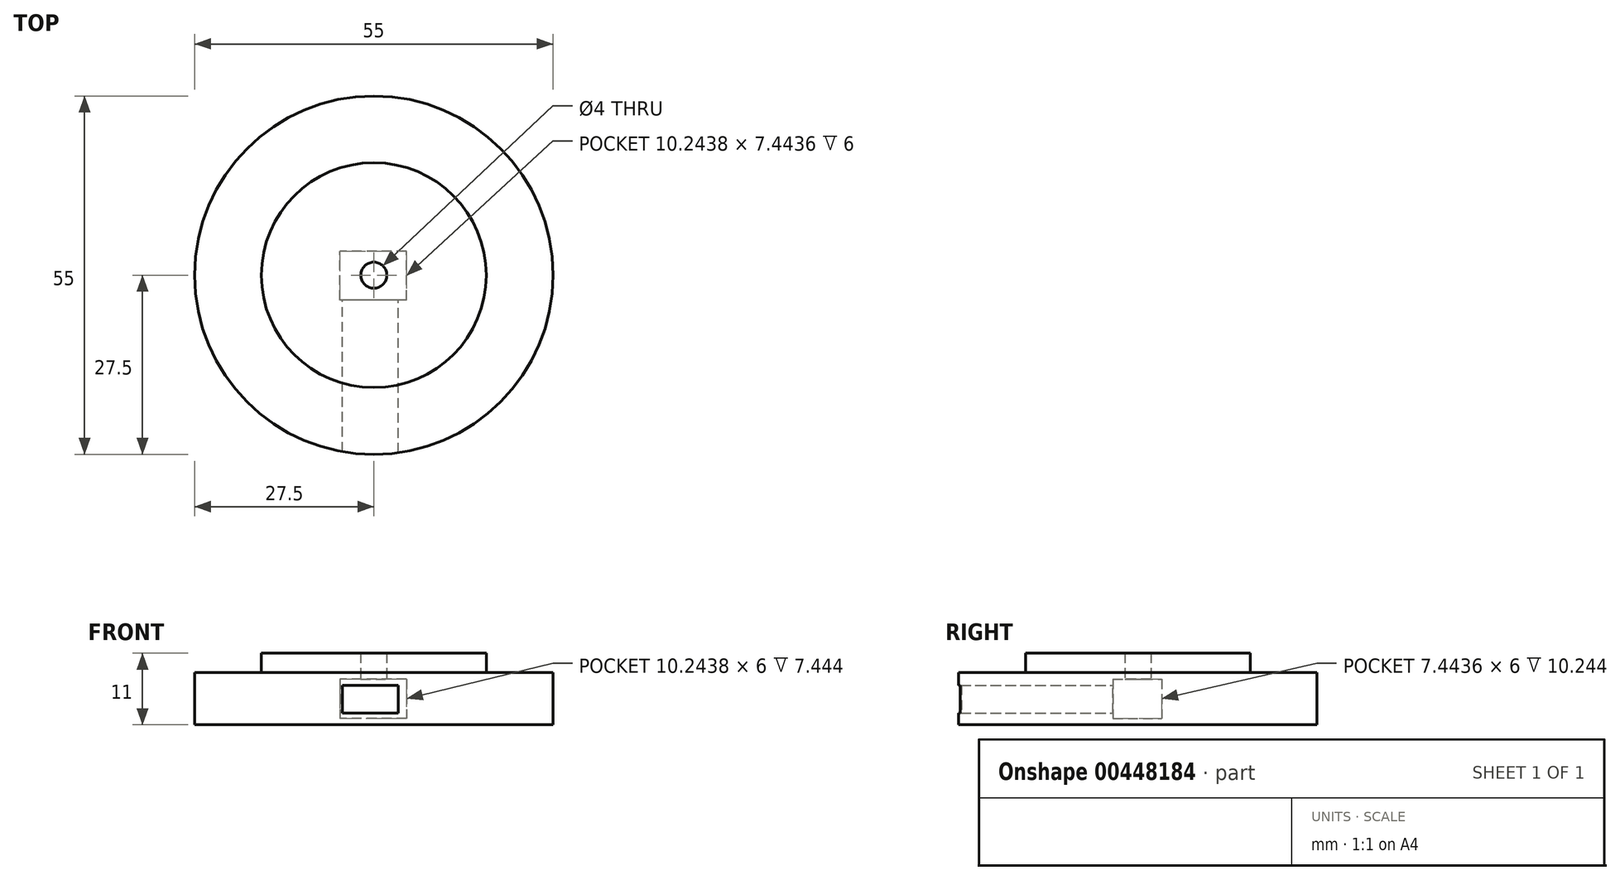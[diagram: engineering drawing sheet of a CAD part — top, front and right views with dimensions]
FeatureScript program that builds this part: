
annotation { "Feature Type Name" : "Feature", "Feature Type Description" : "" }
export const myFeature = defineFeature(function(context is Context, id is Id, definition is map)
    precondition{}
    {
        {
            var Q0;
            Q0=qCreatedBy(makeId("Top.planeOp"),FACE);
            var sketch = newSketch(context, id + "F0", { "sketchPlane" : qUnion([Q0])});
            skCircle(sketch, "E0", {"center": v(0, 0) * mm, "radius": 27.5 * mm});
            skSolve(sketch);
        }
        {
            var Q0;
            Q0=makeQuery(id+"F0.imprint","IMPRINT",FACE,{"disambiguationData":[TD([[makeQuery(id+"F0.imprint","IMPRINT",EDGE,{"derivedFrom":sQuery(id+"F0.wireOp",EDGE,"E0")}),1.0]])]});
            extrude(context, id + "F1", {"entities" : qUnion([Q0]), "depth" : 8 * mm});
        }
        {
            var Q0;
            Q0=makeQuery(id+"F1.opExtrude","CAP_FACE",FACE,{"disambiguationData":[OSD([sQuery(id+"F0.wireOp",EDGE,"E0")])],"isStart":false});
            var sketch = newSketch(context, id + "F2", { "sketchPlane" : qUnion([Q0])});
            skCircle(sketch, "E1", {"center": v(0, 0) * mm, "radius": 17.25 * mm});
            skSolve(sketch);
        }
        {
            var Q0;
            Q0=makeQuery(id+"F2.imprint","IMPRINT",FACE,{"disambiguationData":[TD([[makeQuery(id+"F2.imprint","IMPRINT",EDGE,{"derivedFrom":sQuery(id+"F2.wireOp",EDGE,"E1")}),1.0]])]});
            extrude(context, id + "F3", {"entities" : qUnion([Q0]), "operationType" : NewBodyOperationType.ADD, "depth" : 3 * mm});
        }
        {
            var Q0;
            Q0=makeQuery(id+"F1.opExtrude","CAP_FACE",FACE,{"disambiguationData":[OSD([sQuery(id+"F0.wireOp",EDGE,"E0")])],"isStart":true});
            var sketch = newSketch(context, id + "F4", { "sketchPlane" : qUnion([Q0])});
            skLineSegment(sketch, "E2.bottom", {"start": v(5.02, 3.8) * mm, "end": v(-5.22, 3.8) * mm});
            skLineSegment(sketch, "E2.top", {"start": v(5.02, -3.64) * mm, "end": v(-5.22, -3.64) * mm});
            skLineSegment(sketch, "E2.left", {"start": v(5.02, 3.8) * mm, "end": v(5.02, -3.64) * mm});
            skLineSegment(sketch, "E2.right", {"start": v(-5.22, 3.8) * mm, "end": v(-5.22, -3.64) * mm});
            skSolve(sketch);
        }
        {
            var Q0;
            Q0=makeQuery(id+"F4.imprint","IMPRINT",FACE,{"disambiguationData":[TD([[makeQuery(id+"F4.imprint","IMPRINT",EDGE,{"derivedFrom":sQuery(id+"F4.wireOp",EDGE,"E2.bottom")}),1.0]])]});
            extrude(context, id + "F5", {"entities" : qUnion([Q0]), "operationType" : NewBodyOperationType.REMOVE, "oppositeDirection" : true, "depth" : 7 * mm});
        }
        {
            var Q0;
            Q0=makeQuery(id+"F5.boolean.opBoolean","COPY",FACE,{"derivedFrom":makeQuery(id+"F5.opExtrude","SWEPT_FACE",FACE,{"disambiguationData":[OSD([sQuery(id+"F4.wireOp",EDGE,"E2.bottom")])]})});
            var sketch = newSketch(context, id + "F6", { "sketchPlane" : qUnion([Q0])});
            skLineSegment(sketch, "E3.bottom", {"start": v(-3.75, 1.83) * mm, "end": v(4.8, 1.83) * mm});
            skLineSegment(sketch, "E3.top", {"start": v(-3.75, 6.08) * mm, "end": v(4.8, 6.08) * mm});
            skLineSegment(sketch, "E3.left", {"start": v(-3.75, 1.83) * mm, "end": v(-3.75, 6.08) * mm});
            skLineSegment(sketch, "E3.right", {"start": v(4.8, 1.83) * mm, "end": v(4.8, 6.08) * mm});
            skSolve(sketch);
        }
        {
            var Q0;
            Q0=makeQuery(id+"F6.imprint","IMPRINT",FACE,{"disambiguationData":[TD([[makeQuery(id+"F6.imprint","IMPRINT",EDGE,{"derivedFrom":sQuery(id+"F6.wireOp",EDGE,"E3.bottom")}),1.0]])]});
            extrude(context, id + "F7", {"entities" : qUnion([Q0]), "operationType" : NewBodyOperationType.REMOVE, "oppositeDirection" : true, "depth" : 25 * mm});
        }
        {
            var Q0;
            Q0=makeQuery(id+"F5.boolean.opBoolean","COPY",FACE,{"derivedFrom":makeQuery(id+"F5.opExtrude","CAP_FACE",FACE,{"disambiguationData":[OSD([sQuery(id+"F4.wireOp",EDGE,"E2.bottom"),sQuery(id+"F4.wireOp",EDGE,"E2.top"),sQuery(id+"F4.wireOp",EDGE,"E2.left"),sQuery(id+"F4.wireOp",EDGE,"E2.right")])],"isStart":false})});
            var sketch = newSketch(context, id + "F8", { "sketchPlane" : qUnion([Q0])});
            skCircle(sketch, "E4", {"center": v(0, 0) * mm, "radius": 2 * mm});
            skSolve(sketch);
        }
        {
            var Q0;
            Q0=makeQuery(id+"F8.imprint","IMPRINT",FACE,{"disambiguationData":[TD([[makeQuery(id+"F8.imprint","IMPRINT",EDGE,{"derivedFrom":sQuery(id+"F8.wireOp",EDGE,"E4")}),1.0]])]});
            extrude(context, id + "F9", {"entities" : qUnion([Q0]), "operationType" : NewBodyOperationType.REMOVE, "oppositeDirection" : true, "depth" : 25 * mm});
        }
        {
            var Q0;
            Q0=makeQuery(id+"F1.opExtrude","CAP_FACE",FACE,{"disambiguationData":[OSD([sQuery(id+"F0.wireOp",EDGE,"E0")])],"isStart":true});
            var sketch = newSketch(context, id + "F10", { "sketchPlane" : qUnion([Q0])});
            skLineSegment(sketch, "E5.bottom", {"start": v(5.02, 3.8) * mm, "end": v(-5.22, 3.8) * mm});
            skLineSegment(sketch, "E5.top", {"start": v(5.02, -3.64) * mm, "end": v(-5.22, -3.64) * mm});
            skLineSegment(sketch, "E5.left", {"start": v(5.02, 3.8) * mm, "end": v(5.02, -3.64) * mm});
            skLineSegment(sketch, "E5.right", {"start": v(-5.22, 3.8) * mm, "end": v(-5.22, -3.64) * mm});
            skSolve(sketch);
        }
        {
            var Q0;
            Q0=makeQuery(id+"F10.imprint","IMPRINT",FACE,{"disambiguationData":[TD([[makeQuery(id+"F10.imprint","IMPRINT",EDGE,{"derivedFrom":sQuery(id+"F10.wireOp",EDGE,"E5.bottom")}),1.0]])]});
            extrude(context, id + "F11", {"entities" : qUnion([Q0]), "operationType" : NewBodyOperationType.ADD, "oppositeDirection" : true, "depth" : 1 * mm});
        }
    });
